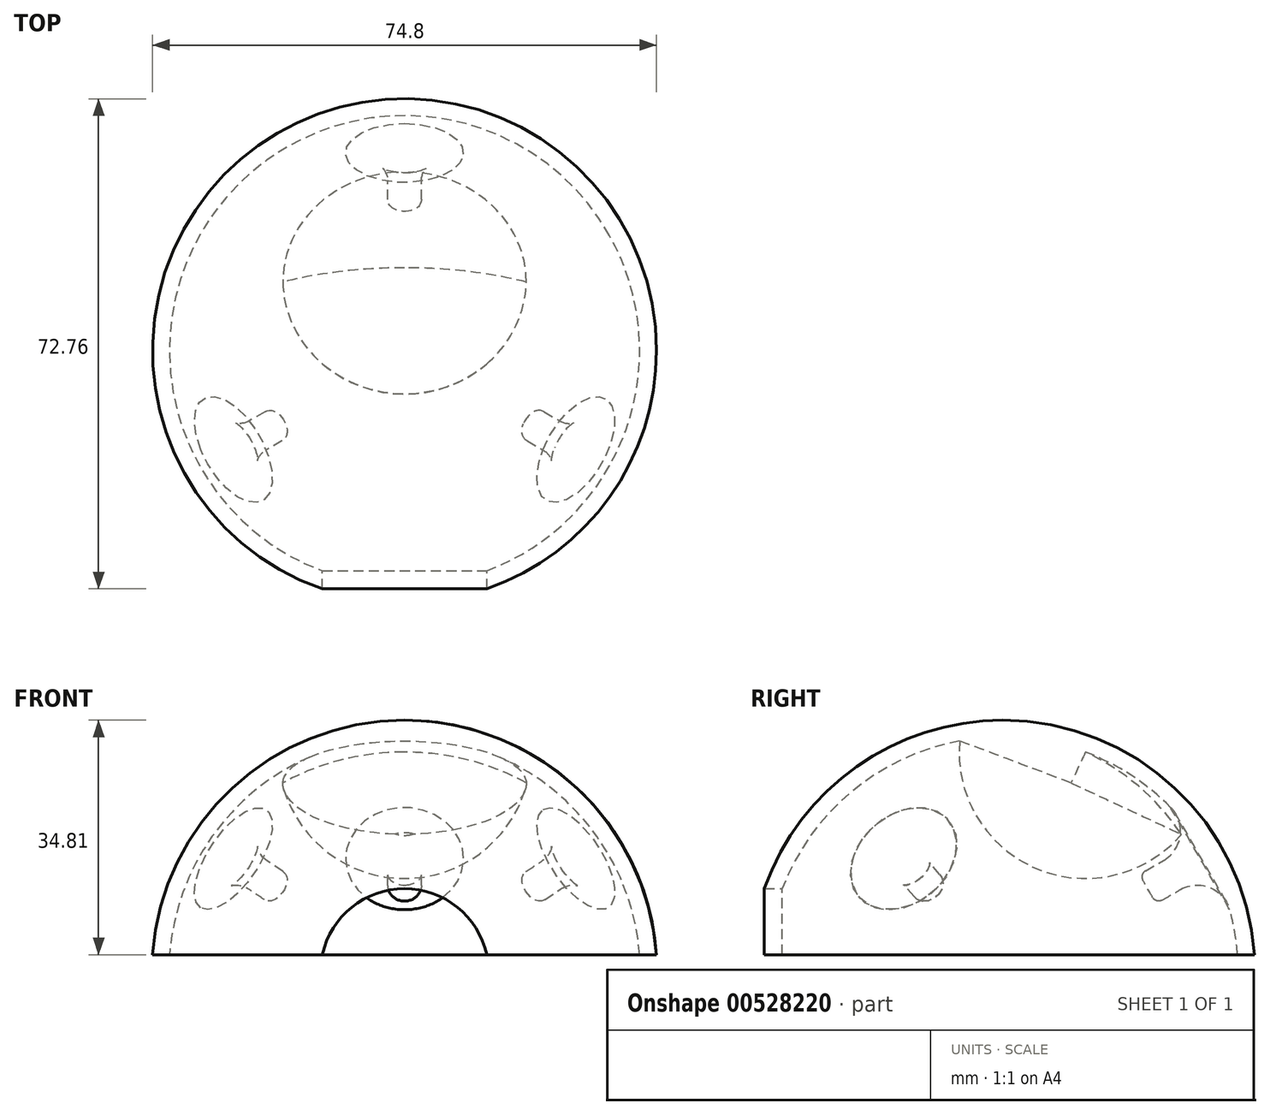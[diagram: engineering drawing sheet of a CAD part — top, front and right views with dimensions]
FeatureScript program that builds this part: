
annotation { "Feature Type Name" : "Feature", "Feature Type Description" : "" }
export const myFeature = defineFeature(function(context is Context, id is Id, definition is map)
    precondition{}
    {
        {
            var Q0;
            Q0=qCreatedBy(makeId("Front.planeOp"),FACE);
            var sketch = newSketch(context, id + "F0", { "sketchPlane" : qUnion([Q0])});
            skArc(sketch, "E0", {"start": v(37.4, 2.7) * mm, "mid": v(25.55, 27.45) * mm, "end": v(0, 37.5) * mm});
            skArc(sketch, "E1", {"start": v(34.9, 2.7) * mm, "mid": v(23.78, 25.68) * mm, "end": v(0, 35) * mm});
            skLineSegment(sketch, "E2", {"start": v(0, 37.5) * mm, "end": v(0, 35) * mm});
            skLineSegment(sketch, "E3.top", {"start": v(37.4, 2.7) * mm, "end": v(34.9, 2.7) * mm});
            skSolve(sketch);
        }
        {
            var Q0;
            Q0=makeQuery(id+"F0.imprint","IMPRINT",FACE,{"disambiguationData":[TD([[makeQuery(id+"F0.imprint","IMPRINT",EDGE,{"derivedFrom":sQuery(id+"F0.wireOp",EDGE,"E0")}),1.0]])]});
            var Q1;
            Q1=sQuery(id+"F0.wireOp",EDGE,"E2");
            revolve(context, id + "F1", {"entities" : qUnion([Q0]), "axis" : qUnion([Q1]), "revolveType" : RevolveType.FULL});
        }
        {
            var Q0;
            Q0=qCreatedBy(makeId("Front.planeOp"),FACE);
            var sketch = newSketch(context, id + "F2", { "sketchPlane" : qUnion([Q0])});
            skCircle(sketch, "E4", {"center": v(0, 0) * mm, "radius": 12.5 * mm});
            skSolve(sketch);
        }
        {
            var Q0;
            Q0=qSketchRegion(id+"F2",true);
            extrude(context, id + "F3", {"entities" : qUnion([Q0]), "operationType" : NewBodyOperationType.REMOVE, "endBound" : BoundingType.THROUGH_ALL, "depth" : 25 * mm, "offsetDistance" : 25 * mm});
        }
        {
            var Q0;
            Q0=makeQuery(id+"F1.opRevolve","SWEPT_EDGE",EDGE,{"disambiguationData":[OSD([sQuery(id+"F0.wireOp",EDGE,"E1"),sQuery(id+"F0.wireOp",EDGE,"E3.top")])]});
            cPoint(context, id + "F4", {"entities" : qUnion([Q0]), "parameter" : 0.5});
        }
        {
            var Q0;
            Q0=qCreatedBy(makeId("Front.planeOp"),FACE);
            var Q1;
            Q1=qCreatedBy(id+"F4",VERTEX);
            cPlane(context, id + "F5", {"entities" : qUnion([Q0, Q1]), "cplaneType" : CPlaneType.PLANE_POINT, "offset" : 25 * mm, "width" : 150 * mm, "height" : 150 * mm});
        }
        {
            var Q0;
            Q0=qCreatedBy(id+"F5.planeOp",FACE);
            var sketch = newSketch(context, id + "F6", { "sketchPlane" : qUnion([Q0])});
            skCircle(sketch, "E5", {"center": v(0, 0) * mm, "radius": 2.5 * mm});
            skSolve(sketch);
        }
        {
            var Q0;
            Q0=qCreatedBy(makeId("Top.planeOp"),FACE);
            var sketch = newSketch(context, id + "F7", { "sketchPlane" : qUnion([Q0])});
            skLineSegment(sketch, "E6", {"start": v(-46.34, 0) * mm, "end": v(50.33, 0) * mm, "construction": true});
            skSolve(sketch);
        }
        {
            var Q0;
            Q0=qSketchRegion(id+"F6",true);
            extrude(context, id + "F8", {"entities" : qUnion([Q0]), "operationType" : NewBodyOperationType.ADD, "depth" : 10 * mm, "offsetDistance" : 25 * mm, "hasSecondDirection" : true, "secondDirectionOppositeDirection" : true, "secondDirectionDepth" : 1 * mm});
        }
        {
            var Q0;
            Q0=makeQuery(id+"F8.opExtrude","SWEPT_BODY",BODY,{"disambiguationData":[OSD([sQuery(id+"F6.wireOp",EDGE,"E5")])]});
            var Q1;
            Q1=sQuery(id+"F7.wireOp",EDGE,"E6");
            transform(context, id + "F9", {"entities" : qUnion([Q0]), "transformType" : TransformType.ROTATION, "transformAxis" : qUnion([Q1]), "angle" : 30 * degree, "makeCopy" : false});
        }
        {
            var Q0;
            Q0=qCreatedBy(makeId("Front.planeOp"),FACE);
            var sketch = newSketch(context, id + "F10", { "sketchPlane" : qUnion([Q0])});
            skLineSegment(sketch, "E7", {"start": v(0, 0) * mm, "end": v(0, 49.93) * mm, "construction": true});
            skSolve(sketch);
        }
        {
            var Q0;
            Q0=makeQuery(id+"F8.opExtrude","SWEPT_BODY",BODY,{"disambiguationData":[OSD([sQuery(id+"F6.wireOp",EDGE,"E5")])]});
            var Q1;
            Q1=sQuery(id+"F10.wireOp",EDGE,"E7");
            circularPattern(context, id + "F11", {"operationType" : NewBodyOperationType.ADD, "entities" : qUnion([Q0]), "axis" : qUnion([Q1]), "angle" : 360 * degree, "instanceCount" : 3, "equalSpace" : true});
        }
        {
            var Q0;
            Q0=makeQuery(id+"F11.boolean.opBoolean","INTERSECT",EDGE,{"derivedFrom":[makeQuery(id+"F1.opRevolve","SWEPT_FACE",FACE,{"disambiguationData":[OSD([sQuery(id+"F0.wireOp",EDGE,"E1")])]}),makeQuery(id+"F11.opPattern","COPY",FACE,{"derivedFrom":makeQuery(id+"F8.opExtrude","SWEPT_FACE",FACE,{"disambiguationData":[OSD([sQuery(id+"F6.wireOp",EDGE,"E5")])]}),"instanceName":"2"})]});
            var Q1;
            Q1=makeQuery(id+"F11.boolean.opBoolean","INTERSECT",EDGE,{"derivedFrom":[makeQuery(id+"F1.opRevolve","SWEPT_FACE",FACE,{"disambiguationData":[OSD([sQuery(id+"F0.wireOp",EDGE,"E1")])]}),makeQuery(id+"F8.opExtrude","SWEPT_FACE",FACE,{"disambiguationData":[OSD([sQuery(id+"F6.wireOp",EDGE,"E5")])]})]});
            var Q2;
            Q2=makeQuery(id+"F11.boolean.opBoolean","INTERSECT",EDGE,{"derivedFrom":[makeQuery(id+"F1.opRevolve","SWEPT_FACE",FACE,{"disambiguationData":[OSD([sQuery(id+"F0.wireOp",EDGE,"E1")])]}),makeQuery(id+"F11.opPattern","COPY",FACE,{"derivedFrom":makeQuery(id+"F8.opExtrude","SWEPT_FACE",FACE,{"disambiguationData":[OSD([sQuery(id+"F6.wireOp",EDGE,"E5")])]}),"instanceName":"1"})]});
            fillet(context, id + "F12", {"entities" : qUnion([Q0, Q1, Q2]), "radius" : 5 * mm, "tangentPropagation" : true, "allowEdgeOverflow" : false});
        }
        {
            var Q0;
            Q0=makeQuery(id+"F11.opPattern","COPY",EDGE,{"derivedFrom":makeQuery(id+"F8.opExtrude","CAP_EDGE",EDGE,{"disambiguationData":[OSD([sQuery(id+"F6.wireOp",EDGE,"E5")])],"isStart":false}),"instanceName":"1"});
            var Q1;
            Q1=makeQuery(id+"F11.opPattern","COPY",EDGE,{"derivedFrom":makeQuery(id+"F8.opExtrude","CAP_EDGE",EDGE,{"disambiguationData":[OSD([sQuery(id+"F6.wireOp",EDGE,"E5")])],"isStart":false}),"instanceName":"2"});
            var Q2;
            Q2=makeQuery(id+"F8.opExtrude","CAP_EDGE",EDGE,{"disambiguationData":[OSD([sQuery(id+"F6.wireOp",EDGE,"E5")])],"isStart":false});
            fillet(context, id + "F13", {"entities" : qUnion([Q0, Q1, Q2]), "radius" : 1 * mm, "tangentPropagation" : true, "allowEdgeOverflow" : false});
        }
        {
            var Q0;
            Q0=makeQuery(id+"F1.opRevolve","SWEPT_FACE",FACE,{"disambiguationData":[OSD([sQuery(id+"F0.wireOp",EDGE,"E3.top")])]});
            var sketch = newSketch(context, id + "F14", { "sketchPlane" : qUnion([Q0])});
            skArc(sketch, "E8.0", {"start": v(18.07, -29.85) * mm, "mid": v(9.38, -33.61) * mm, "end": v(0, -34.9) * mm});
            skArc(sketch, "E9", {"start": v(18.07, -29.85) * mm, "mid": v(11.34, -19.96) * mm, "end": v(0, -16.14) * mm});
            skPoint(sketch, "E10.orphan", {"position": v(-12.2, 32.7) * mm});
            skPoint(sketch, "E11.orphan", {"position": v(12.2, 32.7) * mm});
            skLineSegment(sketch, "E12", {"start": v(0, -34.9) * mm, "end": v(0, -16.14) * mm});
            skSolve(sketch);
        }
        {
            var Q0;
            Q0 = qSketchRegion(id + "F14", true);
            var Q1;
            Q1=makeQuery(id+"F14.imprint","IMPRINT",FACE,{"disambiguationData":[TD([[makeQuery(id+"F14.imprint","IMPRINT",EDGE,{"derivedFrom":sQuery(id+"F14.wireOp",EDGE,"E8.0")}),-1.0]])]});
            var Q2;
            Q2=sQuery(id+"F14.wireOp",EDGE,"E12");
            revolve(context, id + "F15", {"entities" : qUnion([Q0, Q1]), "axis" : qUnion([Q2]), "revolveType" : RevolveType.FULL});
        }
        {
            var Q0;
            Q0=makeQuery(id+"F15.opRevolve","SWEPT_BODY",BODY,{"disambiguationData":[OSD([sQuery(id+"F14.wireOp",EDGE,"E8.0"),sQuery(id+"F14.wireOp",EDGE,"E9"),sQuery(id+"F14.wireOp",EDGE,"E12")])]});
            var Q1;
            Q1=sQuery(id+"F7.wireOp",EDGE,"E6");
            transform(context, id + "F16", {"entities" : qUnion([Q0]), "transformType" : TransformType.ROTATION, "transformAxis" : qUnion([Q1]), "angle" : 65 * degree, "oppositeDirection" : true, "makeCopy" : false});
        }
        {
            var Q0;
            Q0=makeQuery(id+"F15.opRevolve","SWEPT_BODY",BODY,{"disambiguationData":[OSD([sQuery(id+"F14.wireOp",EDGE,"E8.0"),sQuery(id+"F14.wireOp",EDGE,"E9"),sQuery(id+"F14.wireOp",EDGE,"E12")])]});
            var Q1;
            Q1=sQuery(id+"F7.wireOp",EDGE,"E6");
            circularPattern(context, id + "F17", {"operationType" : NewBodyOperationType.ADD, "entities" : qUnion([Q0]), "axis" : qUnion([Q1]), "angle" : 130 * degree, "instanceCount" : 2, "equalSpace" : true});
        }
        {
            var Q0;
            Q0=qCreatedBy(makeId("Right.planeOp"),FACE);
            var sketch = newSketch(context, id + "F18", { "sketchPlane" : qUnion([Q0])});
            skLineSegment(sketch, "E13.bottom", {"start": v(46.76, -4.44) * mm, "end": v(-26.72, -4.44) * mm});
            skLineSegment(sketch, "E13.top", {"start": v(46.76, -46.97) * mm, "end": v(-26.72, -46.97) * mm});
            skLineSegment(sketch, "E13.left", {"start": v(46.76, -4.44) * mm, "end": v(46.76, -46.97) * mm});
            skLineSegment(sketch, "E13.right", {"start": v(-26.72, -4.44) * mm, "end": v(-26.72, -46.97) * mm});
            skSolve(sketch);
        }
        {
            var Q0;
            Q0 = qSketchRegion(id + "F18", true);
            extrude(context, id + "F19", {"entities" : qUnion([Q0]), "operationType" : NewBodyOperationType.REMOVE, "endBound" : BoundingType.THROUGH_ALL, "oppositeDirection" : true, "depth" : 25 * mm, "offsetDistance" : 25 * mm, "hasSecondDirection" : true, "secondDirectionOppositeDirection" : false, "secondDirectionDepth" : 25 * mm});
        }
    });
